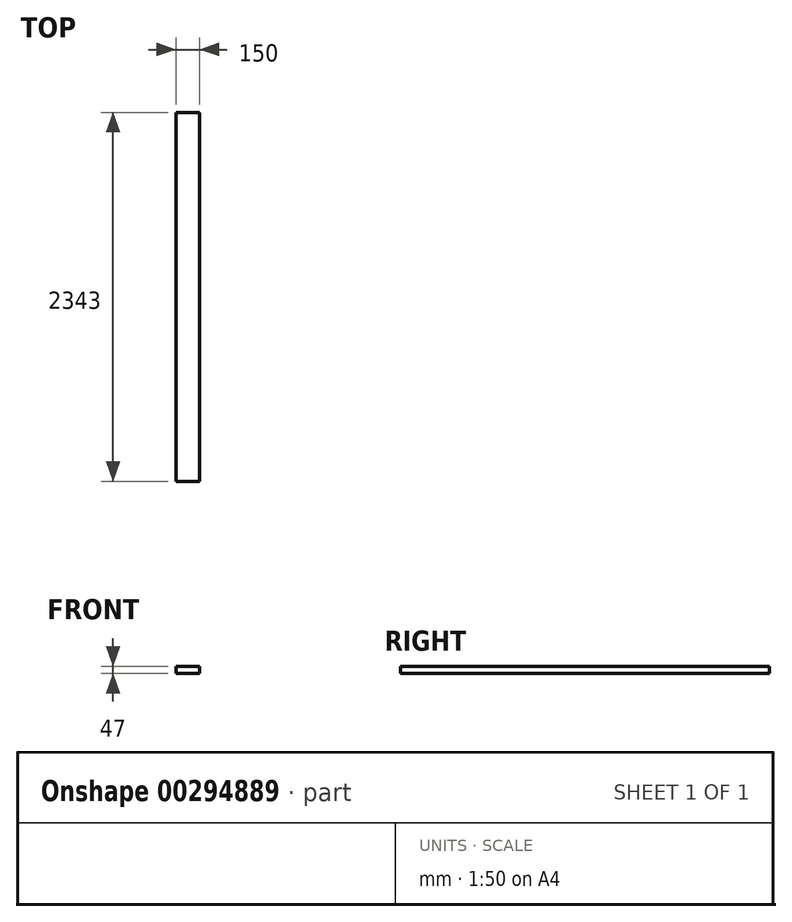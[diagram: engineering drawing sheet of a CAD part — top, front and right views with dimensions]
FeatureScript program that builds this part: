
annotation { "Feature Type Name" : "Feature", "Feature Type Description" : "" }
export const myFeature = defineFeature(function(context is Context, id is Id, definition is map)
    precondition{}
    {
        {
            var Q0;
            Q0=qCreatedBy(makeId("Front.planeOp"),FACE);
            var sketch = newSketch(context, id + "F0", { "sketchPlane" : qUnion([Q0])});
            skLineSegment(sketch, "E0.bottom", {"start": v(75, 23.5) * mm, "end": v(-75, 23.5) * mm});
            skLineSegment(sketch, "E0.top", {"start": v(75, -23.5) * mm, "end": v(-75, -23.5) * mm});
            skLineSegment(sketch, "E0.left", {"start": v(75, 23.5) * mm, "end": v(75, -23.5) * mm});
            skLineSegment(sketch, "E0.right", {"start": v(-75, 23.5) * mm, "end": v(-75, -23.5) * mm});
            skPoint(sketch, "E0.middle", {"position": v(0, 0) * mm});
            skSolve(sketch);
        }
        {
            var Q0;
            Q0 = qSketchRegion(id + "F0", true);
            extrude(context, id + "F1", {"entities" : qUnion([Q0]), "depth" : (2600 - 94 - 163) * mm});
        }
    });
